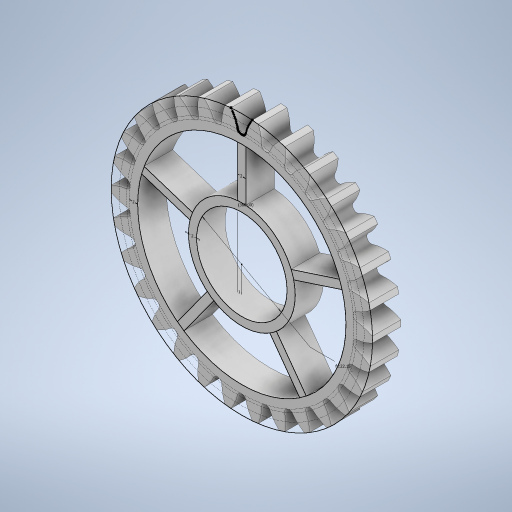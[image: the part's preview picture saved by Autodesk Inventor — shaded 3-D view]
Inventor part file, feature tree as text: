
AUTODESK INVENTOR PART (.ipt)
format: ipt  version: 2023 (Build 270158000, 158)  size: 497,152 bytes
history: native  units: mm
features: extrude x2, sketch x1, pattern_circular x1
ambient origin geometry x8: Origin, YZ Plane, XZ Plane, XY Plane, X Axis, Y Axis, Z Axis, Center Point
bodies: Solid1 (feature_tree)
feature tree (4):
  sketch  "Sketch1"  dims[d0=7.0mm d1=0.0mm d2=2.0mm d3=22.15mm d4=2.0mm d5=1.0mm d6=2.0mm d7=50.0mm d9=360.0deg d11=0.0mm d12=0.0mm d13=300.0mm d14=360.0deg]
  extrude  "Extrusion1"  Depth=2.0mm
  extrude  "Extrusion2"  Depth=22.15mm
  pattern_circular  "Circular Pattern1"  [2 undecoded]
note: 2 required parameter values undecoded (feature->parameter linkage not recoverable at this tier; creation-order binding heuristic only, values carry confidence <= 0.55)
